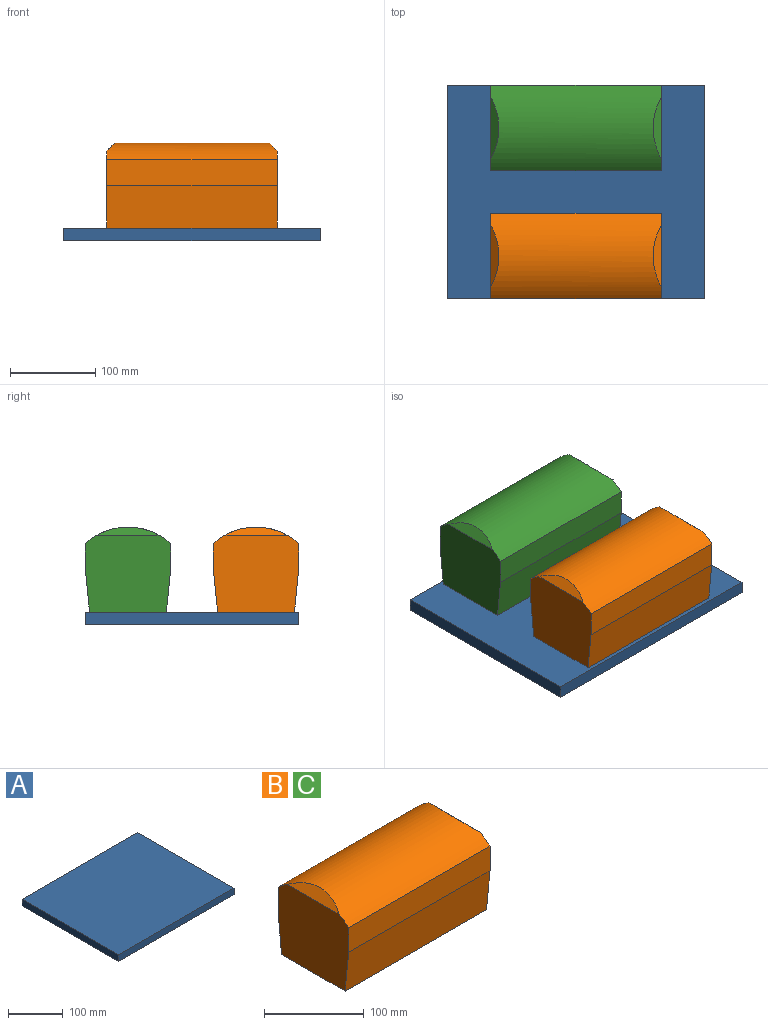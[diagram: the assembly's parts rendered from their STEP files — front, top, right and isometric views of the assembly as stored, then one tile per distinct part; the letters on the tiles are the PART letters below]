
ASSEMBLY  parts=3 mates=4
PART A: 6 faces, bbox 300x250x15 mm
  f0: plane 250x15mm, normal (1,0,0), area 3750mm2, adj f1,f3,f4,f5
  f1: plane 300x15mm, normal (0,1,0), area 4500mm2, adj f0,f2,f4,f5
  f2: plane 250x15mm, normal (-1,0,0), area 3750mm2, adj f1,f3,f4,f5
  f3: plane 300x15mm, normal (0,-1,0), area 4500mm2, adj f0,f2,f4,f5
  f4: plane 300x250mm, normal (0,0,1), area 75000mm2, adj f0,f1,f2,f3
  f5: plane 300x250mm, normal (0,0,-1), area 75000mm2, adj f0,f1,f2,f3
PART B: 10 faces, bbox 200x100x99.6 mm
  f0: plane 100x90mm, normal (1,0,0), area 8624.5mm2, adj f1,f4,f5,f6,f7,f8,f9
  f1: plane 200x30mm, normal (0,1,0), area 6000mm2, adj f0,f2,f8,f9
  f2: plane 100x90mm, normal (-1,0,0), area 8624.5mm2, adj f1,f3,f5,f6,f7,f8,f9
  f3: plane 72.69x9.61mm, normal (-0.71,0,0.71), area 667.4mm2, adj f2,f9
  f4: plane 72.69x9.61mm, normal (0.71,0,0.71), area 667.4mm2, adj f0,f9
  f5: plane 200x30mm, normal (0,-1,0), area 6000mm2, adj f0,f2,f7,f9
  f6: plane 200x90mm, normal (0,0,-1), area 18000mm2, adj f0,f2,f7,f8
  f7: plane 200x50mm, normal (0,-1,-0.1), area 10049.9mm2, adj f0,f2,f5,f6
  f8: plane 200x50mm, normal (0,1,-0.1), area 10049.9mm2, adj f0,f1,f2,f6
  f9: cylinder r=73.56mm len=200mm, axis (1,0,0), area 21021.5mm2, adj f0,f1,f2,f3,f4,f5
PART C: same geometry as B
PLACE A t=(0,-1.1,0)mm
PLACE B t=(0,-76.1,15)mm
PLACE C t=(0,73.9,15)mm
MATE planar B.f6 <-> A.f4  axis (0,0,-1) through (0,-76.1,15)mm
MATE planar B.f5 <-> A.f3  axis (0,-1,0) through (0,-126.1,80)mm
MATE planar C.f6 <-> A.f4  axis (0,0,-1) through (0,73.9,15)mm
MATE parallel C.f5 <-> B.f1  axis (0,-1,0) through (0,23.9,80)mm
